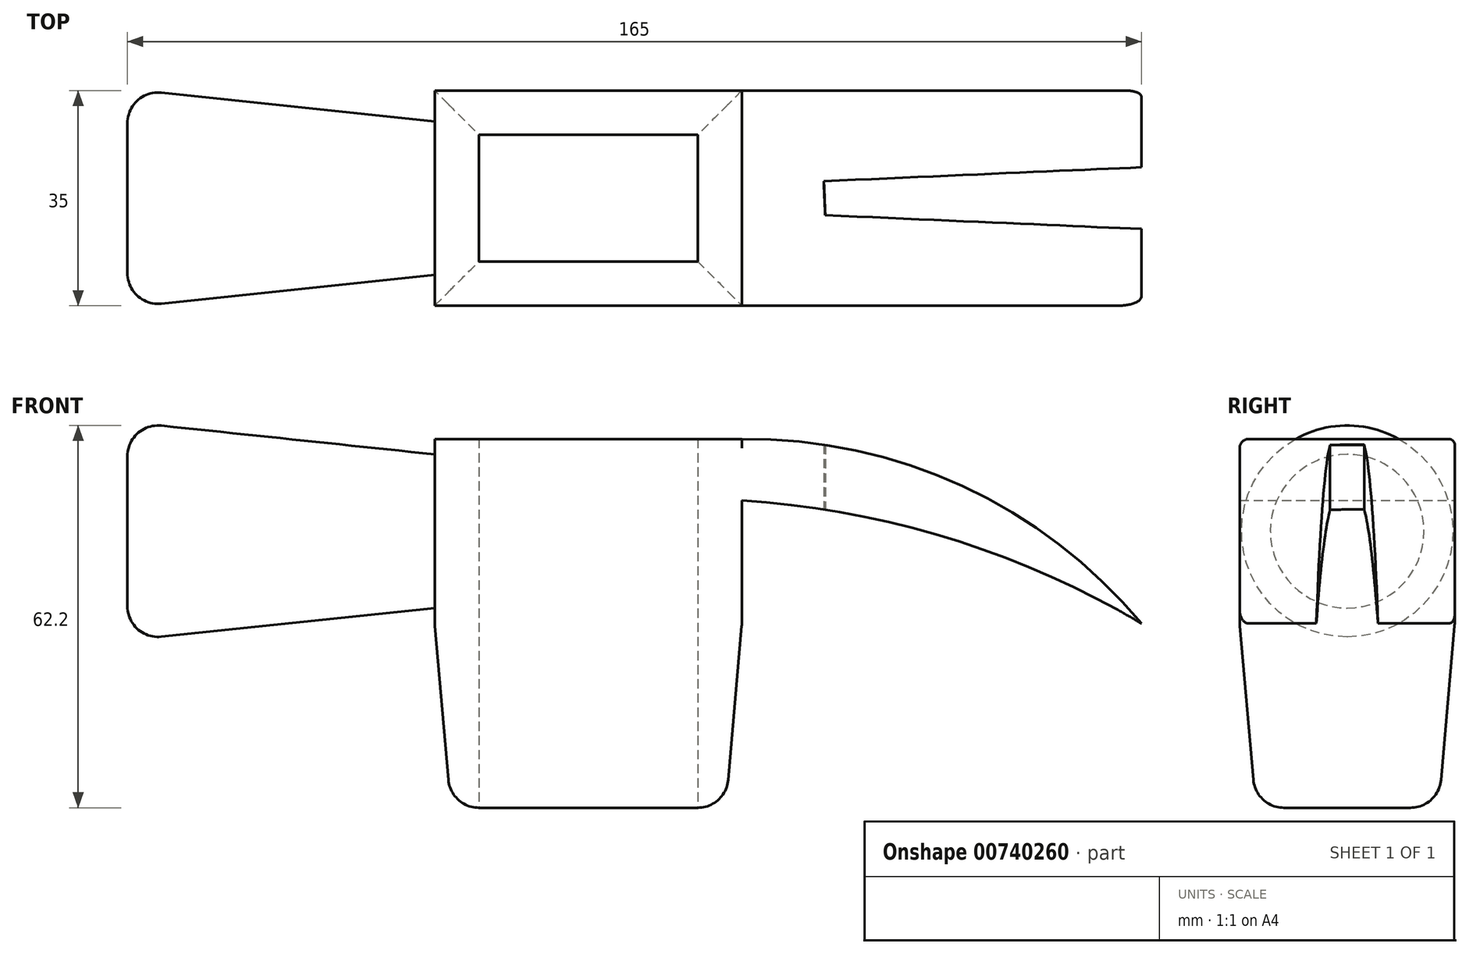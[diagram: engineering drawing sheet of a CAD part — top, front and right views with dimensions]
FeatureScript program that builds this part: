
annotation { "Feature Type Name" : "Feature", "Feature Type Description" : "" }
export const myFeature = defineFeature(function(context is Context, id is Id, definition is map)
    precondition{}
    {
        {
            var Q0;
            Q0=qCreatedBy(makeId("Front.planeOp"),FACE);
            var sketch = newSketch(context, id + "F0", { "sketchPlane" : qUnion([Q0])});
            skLineSegment(sketch, "E0.bottom", {"start": v(0, 0) * mm, "end": v(50, 0) * mm});
            skLineSegment(sketch, "E0.top", {"start": v(0, 30) * mm, "end": v(50, 30) * mm});
            skLineSegment(sketch, "E0.left", {"start": v(0, 0) * mm, "end": v(0, 30) * mm});
            skLineSegment(sketch, "E0.right", {"start": v(50, 0) * mm, "end": v(50, 30) * mm});
            skSolve(sketch);
        }
        {
            var Q0;
            Q0 = qSketchRegion(id + "F0", true);
            extrude(context, id + "F1", {"entities" : qUnion([Q0]), "endBound" : BoundingType.SYMMETRIC, "depth" : 35 * mm, "offsetDistance" : 25 * mm});
        }
        {
            var Q0;
            Q0=makeQuery(id+"F1.opExtrude","SWEPT_FACE",FACE,{"disambiguationData":[OSD([sQuery(id+"F0.wireOp",EDGE,"E0.bottom")])]});
            extrude(context, id + "F2", {"entities" : qUnion([Q0]), "operationType" : NewBodyOperationType.ADD, "depth" : 30 * mm, "offsetDistance" : 25 * mm, "hasDraft" : true, "draftAngle" : 5 * degree, "draftPullDirection" : true});
        }
        {
            var Q0;
            Q0=qCreatedBy(makeId("Right.planeOp"),FACE);
            var sketch = newSketch(context, id + "F3", { "sketchPlane" : qUnion([Q0])});
            skCircle(sketch, "E1", {"center": v(0, 15) * mm, "radius": 12.5 * mm});
            skSolve(sketch);
        }
        {
            var Q0;
            Q0 = qSketchRegion(id + "F3", true);
            extrude(context, id + "F4", {"entities" : qUnion([Q0]), "operationType" : NewBodyOperationType.ADD, "oppositeDirection" : true, "depth" : 50 * mm, "offsetDistance" : 25 * mm, "hasDraft" : true, "draftAngle" : 6 * degree});
        }
        {
            var Q0;
            Q0=qCreatedBy(makeId("Front.planeOp"),FACE);
            var sketch = newSketch(context, id + "F5", { "sketchPlane" : qUnion([Q0])});
            skArc(sketch, "E2", {"start": v(115, 0) * mm, "mid": v(85.89, 22.34) * mm, "end": v(50, 30) * mm});
            skArc(sketch, "E3", {"start": v(115, 0) * mm, "mid": v(83.69, 13.85) * mm, "end": v(50, 20) * mm});
            skLineSegment(sketch, "E4", {"start": v(50, 20) * mm, "end": v(50, 30) * mm});
            skSolve(sketch);
        }
        {
            var Q0;
            Q0 = qSketchRegion(id + "F5", true);
            extrude(context, id + "F6", {"entities" : qUnion([Q0]), "operationType" : NewBodyOperationType.ADD, "endBound" : BoundingType.SYMMETRIC, "depth" : 35 * mm, "offsetDistance" : 25 * mm});
        }
        {
            var Q0;
            Q0=qCreatedBy(makeId("Top.planeOp"),FACE);
            var sketch = newSketch(context, id + "F7", { "sketchPlane" : qUnion([Q0])});
            skLineSegment(sketch, "E5", {"start": v(63.33, 2.77) * mm, "end": v(115.15, 5.03) * mm});
            skLineSegment(sketch, "E6", {"start": v(63.58, -2.78) * mm, "end": v(115.15, -5.03) * mm});
            skLineSegment(sketch, "E7", {"start": v(63.33, 2.77) * mm, "end": v(63.58, -2.78) * mm});
            skLineSegment(sketch, "E8", {"start": v(115.15, 5.03) * mm, "end": v(115.15, -5.03) * mm});
            skSolve(sketch);
        }
        {
            var Q0;
            Q0 = qSketchRegion(id + "F7", true);
            extrude(context, id + "F8", {"entities" : qUnion([Q0]), "operationType" : NewBodyOperationType.REMOVE, "depth" : 62.1 * mm, "offsetDistance" : 25 * mm});
        }
        {
            var Q0;
            Q0=makeQuery(id+"F4.opExtrude","CAP_EDGE",EDGE,{"disambiguationData":[OSD([sQuery(id+"F3.wireOp",EDGE,"E1")])],"isStart":false});
            fillet(context, id + "F9", {"entities" : qUnion([Q0]), "radius" : 5 * mm, "tangentPropagation" : true, "allowEdgeOverflow" : false});
        }
        {
            var Q0;
            {var subQ0=sQuery(id+"F0.wireOp",EDGE,"E0.bottom");var subQ1=makeQuery(id+"F1.opExtrude","CAP_EDGE",EDGE,{"disambiguationData":[OSD([subQ0])],"isStart":false});Q0=makeQuery(id+"F2.boolean.opBoolean","MERGE",EDGE,{"derivedFrom":[subQ1,makeQuery(id+"F2.opExtrude","CAP_EDGE",EDGE,{"disambiguationData":[OSD([subQ0]),TDD([subQ1])],"isStart":true})]});}
            var Q1;
            {var subQ0=sQuery(id+"F0.wireOp",EDGE,"E0.left");var subQ1=sQuery(id+"F0.wireOp",EDGE,"E0.bottom");Q1=makeQuery(id+"F2.boolean.opBoolean","MERGE",EDGE,{"derivedFrom":[makeQuery(id+"F1.opExtrude","SWEPT_EDGE",EDGE,{"disambiguationData":[OSD([subQ1,subQ0])]}),makeQuery(id+"F2.opExtrude","CAP_EDGE",EDGE,{"disambiguationData":[OSD([subQ1,subQ0])],"isStart":true})]});}
            var Q2;
            {var subQ0=sQuery(id+"F0.wireOp",EDGE,"E0.right");var subQ1=sQuery(id+"F0.wireOp",EDGE,"E0.bottom");Q2=makeQuery(id+"F2.boolean.opBoolean","MERGE",EDGE,{"derivedFrom":[makeQuery(id+"F1.opExtrude","SWEPT_EDGE",EDGE,{"disambiguationData":[OSD([subQ1,subQ0])]}),makeQuery(id+"F2.opExtrude","CAP_EDGE",EDGE,{"disambiguationData":[OSD([subQ1,subQ0])],"isStart":true})]});}
            var Q3;
            {var subQ0=sQuery(id+"F0.wireOp",EDGE,"E0.bottom");var subQ1=makeQuery(id+"F1.opExtrude","CAP_EDGE",EDGE,{"disambiguationData":[OSD([subQ0])],"isStart":true});Q3=makeQuery(id+"F2.boolean.opBoolean","MERGE",EDGE,{"derivedFrom":[subQ1,makeQuery(id+"F2.opExtrude","CAP_EDGE",EDGE,{"disambiguationData":[OSD([subQ0]),TDD([subQ1])],"isStart":true})]});}
            fillet(context, id + "F10", {"entities" : qUnion([Q0, Q1, Q2, Q3]), "radius" : 10 * mm, "tangentPropagation" : true, "allowEdgeOverflow" : false});
        }
        {
            var Q0;
            Q0=makeQuery(id+"F2.opExtrude","CAP_EDGE",EDGE,{"disambiguationData":[OSD([sQuery(id+"F0.wireOp",EDGE,"E0.bottom"),sQuery(id+"F0.wireOp",EDGE,"E0.left")])],"isStart":false});
            var Q1;
            {var subQ0=sQuery(id+"F0.wireOp",EDGE,"E0.bottom");Q1=makeQuery(id+"F2.opExtrude","CAP_EDGE",EDGE,{"disambiguationData":[OSD([subQ0]),TDD([makeQuery(id+"F1.opExtrude","CAP_EDGE",EDGE,{"disambiguationData":[OSD([subQ0])],"isStart":true})])],"isStart":false});}
            var Q2;
            Q2=makeQuery(id+"F2.opExtrude","CAP_EDGE",EDGE,{"disambiguationData":[OSD([sQuery(id+"F0.wireOp",EDGE,"E0.bottom"),sQuery(id+"F0.wireOp",EDGE,"E0.right")])],"isStart":false});
            var Q3;
            {var subQ0=sQuery(id+"F0.wireOp",EDGE,"E0.bottom");Q3=makeQuery(id+"F2.opExtrude","CAP_EDGE",EDGE,{"disambiguationData":[OSD([subQ0]),TDD([makeQuery(id+"F1.opExtrude","CAP_EDGE",EDGE,{"disambiguationData":[OSD([subQ0])],"isStart":false})])],"isStart":false});}
            fillet(context, id + "F11", {"entities" : qUnion([Q0, Q1, Q2, Q3]), "radius" : 5 * mm, "tangentPropagation" : true, "allowEdgeOverflow" : false});
        }
        {
            var Q0;
            Q0=makeQuery(id+"F8.boolean.opBoolean","INTERSECT",EDGE,{"derivedFrom":[makeQuery(id+"F6.opExtrude","SWEPT_FACE",FACE,{"disambiguationData":[OSD([sQuery(id+"F5.wireOp",EDGE,"E2")])]}),makeQuery(id+"F8.opExtrude","SWEPT_FACE",FACE,{"disambiguationData":[OSD([sQuery(id+"F7.wireOp",EDGE,"E7")])]})]});
            fillet(context, id + "F12", {"entities" : qUnion([Q0]), "radius" : 0.03 * mm, "tangentPropagation" : true, "allowEdgeOverflow" : false});
        }
        {
            var Q0;
            Q0=makeQuery(id+"F2.opExtrude","CAP_FACE",FACE,{"disambiguationData":[OSD([sQuery(id+"F0.wireOp",EDGE,"E0.bottom")])],"isStart":false});
            extrude(context, id + "F13", {"entities" : qUnion([Q0]), "operationType" : NewBodyOperationType.REMOVE, "oppositeDirection" : true, "depth" : 81.3 * mm, "offsetDistance" : 25 * mm});
        }
        {
            var Q0;
            Q0=makeQuery(id+"F6.opExtrude","CAP_EDGE",EDGE,{"disambiguationData":[OSD([sQuery(id+"F5.wireOp",EDGE,"E2")])],"isStart":true});
            fillet(context, id + "F14", {"entities" : qUnion([Q0]), "radius" : 0.97 * mm, "tangentPropagation" : true, "allowEdgeOverflow" : false});
        }
        {
            var Q0;
            Q0=makeQuery(id+"F6.opExtrude","CAP_EDGE",EDGE,{"disambiguationData":[OSD([sQuery(id+"F5.wireOp",EDGE,"E2")])],"isStart":false});
            fillet(context, id + "F15", {"entities" : qUnion([Q0]), "radius" : 1.45 * mm, "tangentPropagation" : true, "allowEdgeOverflow" : false});
        }
    });
